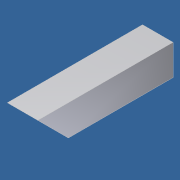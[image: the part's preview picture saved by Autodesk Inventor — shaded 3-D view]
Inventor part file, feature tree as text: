
AUTODESK INVENTOR PART (.ipt)
format: ipt  version: 2012 (Build 160160000, 160)  size: 77,824 bytes
history: native  units: in
note: dims shown in document units (in); Inventor stores cm internally (conversion verified against a paired STEP export)
features: extrude x1, draft x1, sketch x1
ambient origin geometry x8: Origin, YZ Plane, XZ Plane, XY Plane, X Axis, Y Axis, Z Axis, Center Point
bodies: Solid1 (feature_tree)
feature tree (3):
  extrude  "Extrusion1"  Depth=1.75in
  draft  "FaceDraft1"
  sketch  "Sketch1"  dims[d0=0.125in d1=1.75in d2=7.75in d3=0.0in d4=45.0deg]
